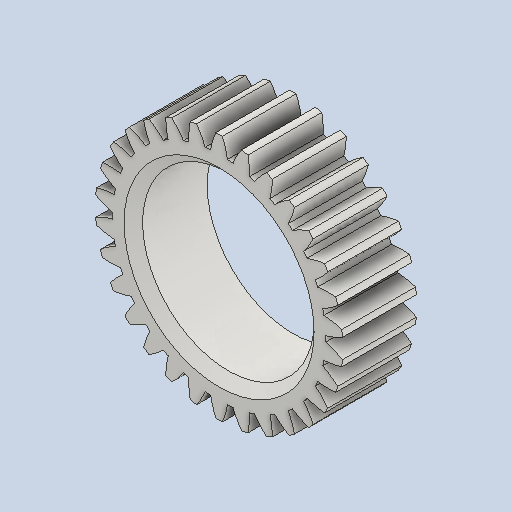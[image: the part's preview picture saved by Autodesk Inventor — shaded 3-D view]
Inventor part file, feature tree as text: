
AUTODESK INVENTOR PART (.ipt)
format: ipt  version: 2022 (Build 260153000, 153)  size: 632,832 bytes
history: native  units: mm (DEFAULTED — no unit token found)
features: plane x4, other x3, sketch x3, extrude x2, chamfer x1
ambient origin geometry x8: Origin, YZ Plane, XZ Plane, XY Plane, X Axis, Y Axis, Z Axis, Center Point
bodies: Solid1 (feature_tree)
feature tree (13):
  extrude  "Extrusion1"  Depth=9.525mm TaperAngle=0.0deg
  plane  "Work Plane1"
  plane  "Work Plane2"
  plane  "Work Plane3"
  other  "Spur Gear"
  extrude  "Extrusion2"  Depth=76.2mm TaperAngle=0.0deg
  plane  "Work Plane4"
  chamfer  "Chamfer1"  Distance=1.047198mm
  sketch  "Sketch1"  dims[d0=31.912126mm d1=9.525mm d2=0.0mm]
  sketch  "Sketch2"  dims[d3=30.0mm d4=76.2mm d5=0.0mm d6=0.0mm d7=1.047198mm]
  other  "Srf1"
  sketch  "Sketch3"  dims[d9=0.0mm d14=0.0mm d15=25.4mm d16=0.0mm d17=0.0mm d18=0.0mm d19=25.4mm d20=22.1mm d21=0.0mm d22=0.0mm d26=1.2mm d27=3.175mm d28=45.0deg]
  other  "Pitch Diameter"
